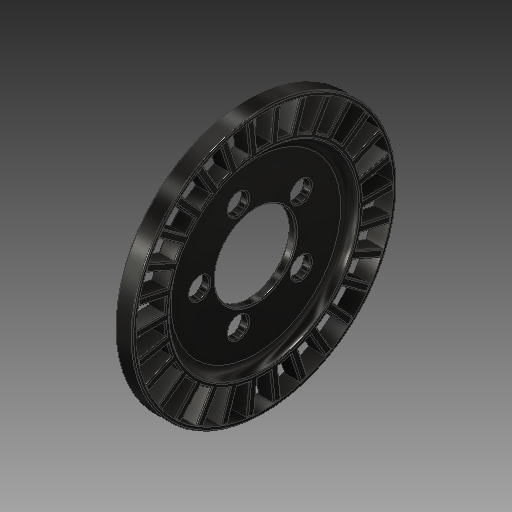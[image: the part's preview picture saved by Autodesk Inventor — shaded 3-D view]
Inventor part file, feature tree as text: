
AUTODESK INVENTOR PART (.ipt)
format: ipt  version: 2019 (Build 230136000, 136)  size: 1,932,800 bytes
history: native  units: mm
features: extrude x5, sketch x5, fillet x2, pattern_circular x2, plane x1, other x1
ambient origin geometry x8: Origin, YZ Plane, XZ Plane, XY Plane, X Axis, Y Axis, Z Axis, Center Point
bodies: Body1 (feature_tree)
feature tree (16):
  extrude  "Extrusion1"  Depth=13.5mm TaperAngle=0.0deg
  plane  "Work Plane1"
  extrude  "Extrusion2"  Depth=0.3mm
  extrude  "Extrusion3"  Depth=14.1mm TaperAngle=0.0deg
  fillet  "Fillet1"  Radius=152.0mm
  extrude  "Extrusion4"  Depth=8.0mm
  pattern_circular  "Circular Pattern1"  [2 undecoded]
  extrude  "Extrusion5"  Depth=1.0mm TaperAngle=0.0deg
  pattern_circular  "Circular Pattern2"  Count=30 Angle=360.0deg
  other  "Rule Fillet2"
  fillet  "Fillet3"  Radius=90.0mm
  sketch  "Sketch1"  dims[d1=65.0mm d14=13.5mm d15=0.0mm]
  sketch  "Sketch2"  dims[d16=0.3mm d17=212.5mm]
  sketch  "Sketch3"  dims[d18=206.5mm d19=14.1mm d20=0.0mm d21=152.0mm]
  sketch  "Sketch4"  dims[d22=6.85mm d23=0.0mm d24=8.0mm]
  sketch  "Sketch5"  dims[d25=6.0mm d26=25.0mm d27=6.85mm d28=0.0mm d29=300.0mm d30=360.0deg d34=90.0mm d37=16.0mm d38=10.0mm d39=0.0mm d40=50.0mm d41=360.0deg d43=1.0mm d44=1.0mm d45=159.5mm]
note: 2 required parameter values undecoded (feature->parameter linkage not recoverable at this tier; creation-order binding heuristic only, values carry confidence <= 0.55)
